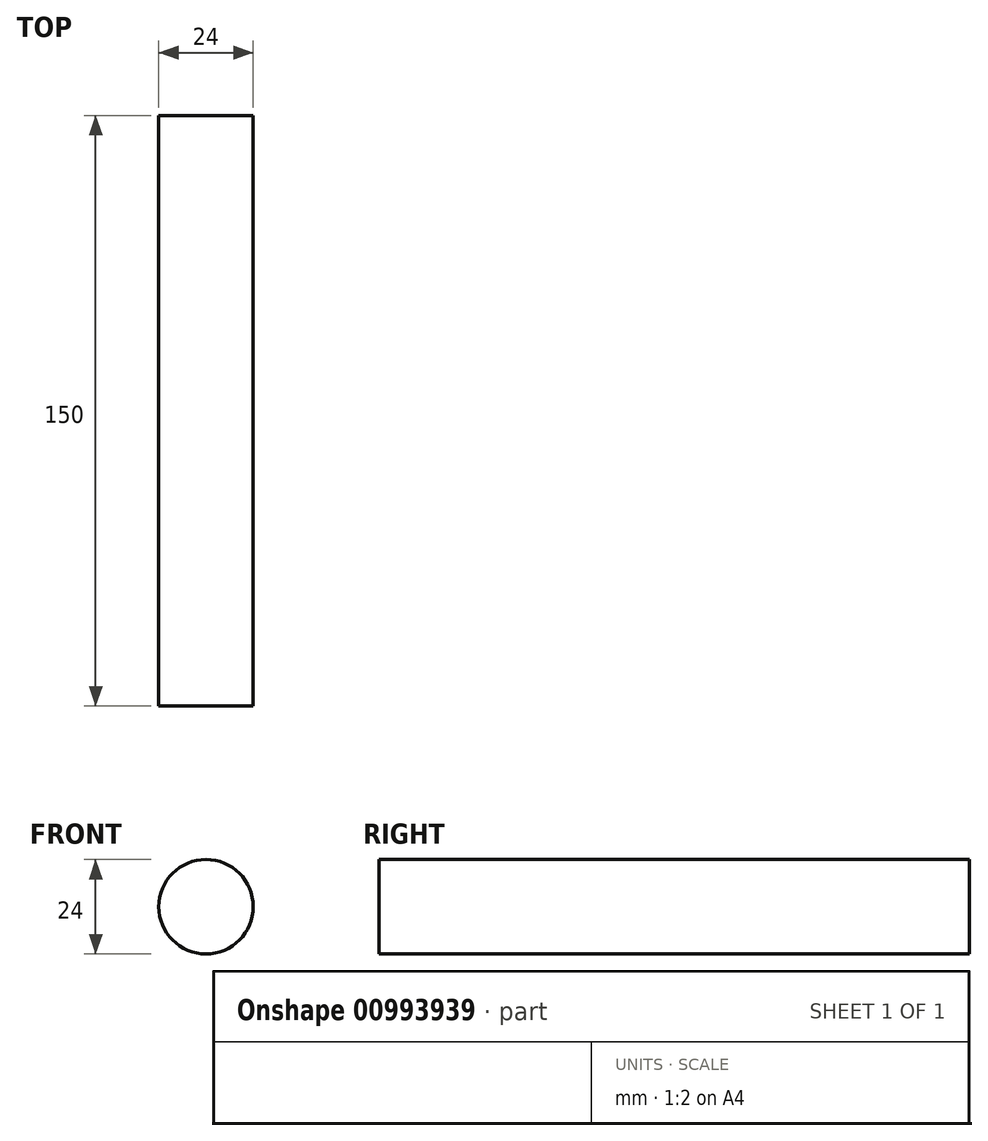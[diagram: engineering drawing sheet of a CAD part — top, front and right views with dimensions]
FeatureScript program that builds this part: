
annotation { "Feature Type Name" : "Feature", "Feature Type Description" : "" }
export const myFeature = defineFeature(function(context is Context, id is Id, definition is map)
    precondition{}
    {
        {
            var Q0;
            Q0=qCreatedBy(makeId("Front.planeOp"),FACE);
            var sketch = newSketch(context, id + "F0", { "sketchPlane" : qUnion([Q0])});
            skCircle(sketch, "E0", {"center": v(-52.8, 24.01) * mm, "radius": 12 * mm});
            skSolve(sketch);
        }
        {
            var Q0;
            Q0=makeQuery(id+"F0.imprint","IMPRINT",FACE,{"disambiguationData":[TD([[makeQuery(id+"F0.imprint","IMPRINT",EDGE,{"derivedFrom":sQuery(id+"F0.wireOp",EDGE,"E0")}),1.0]])]});
            extrude(context, id + "F1", {"entities" : qUnion([Q0]), "depth" : 150 * mm, "offsetDistance" : 25 * mm});
        }
    });
